# Revit family: LIXIL - 709300WH - COBRA SHELTER BASIN WALL HUNG 495X430X190
name_source: partatom
category: Plumbing Fixtures
units: mm (PartAtom-declared; Revit-internal decimal feet)

## family parameters
Always vertical = Yes
Cut with Voids When Loaded = No
Enable Cutting in Views = No
Maintain Annotation Orientation = No
OmniClass Number = 23.45.00.00
OmniClass Title = Sanitary, Laundry, and Cleaning Equipment
Part Type = Normal
Room Calculation Point = No
Round Connector Dimension = Use Diameter
Shared = Yes
Work Plane-Based = No

## types (1)
- 709300WH
    CW Connection Diameter = 55 mm
    CW Connection Radius = 28 mm
    Default Elevation = 0 mm  [stored 0 ft]
    Description = Cobra Shelter 495mm(w) x 430mm(d) x 190mm(h) wall hung basin to detail and spec. See sanware schedule. Available from Lixil.
    Hosted on lixil.co.za = https://www.lixil.co.za
    M _ BASIN = M _ LIXIL - VAAL - PORCELAIN - WHITE 01
    M _ POP UP WASTE = M _ LIXIL - STAINLESS STEEL 01
    Product Specification = Supplier: Lixil.
Product Description: Cobra Shelter Round wall hung basin. 495mm long X 430mm wide. 1 X pre-punched tap hole in the centre of the basin. Overflow, expansion bolts & installation manual included. Compatible with Cobra round full pedestal [CWLPERD1-6DT01] and round semi-pedestal [CWLPERD2-6DT01]. Also compatible with Cobra standard-sized basin mixers.
10 Year Warranty Cobra Genuine Cobra TeamAssist
Product Code: CSHBAWH2-6DT01.
SKU Code	: 709300WH.
Barcode: 6002194040330.
Brand: Cobra.
Range: Shelter.
Category: Basins.
Sub-Category: Wall-hung.
Material: Ceramic.
Colour: White.
Package Height: 220 mm
Package Width: 480 mm
Package Length: 540 mm
Product Height: 190 mm
Product Width: 430 mm
Product Length: 495 mm
Package Volume: 57024000 mm³.
Package Weight: 13.72 kg

Notes:
- Refer to manufacturer's and supplier's installation, maintenance and cleaning manual.
- Refer to manufacturer's and supplier's guarantees and warrantees document.
    Waste Connection Diameter = 102 mm
    Waste Connection Radius = 51 mm

note: [stored X ft] marks values corroborated as IEEE doubles in the binary element streams (Revit-internal decimal feet)

## geometry (parser evidence)
native form markers: Sweep x12
no freeform markers — native parametric forms only
